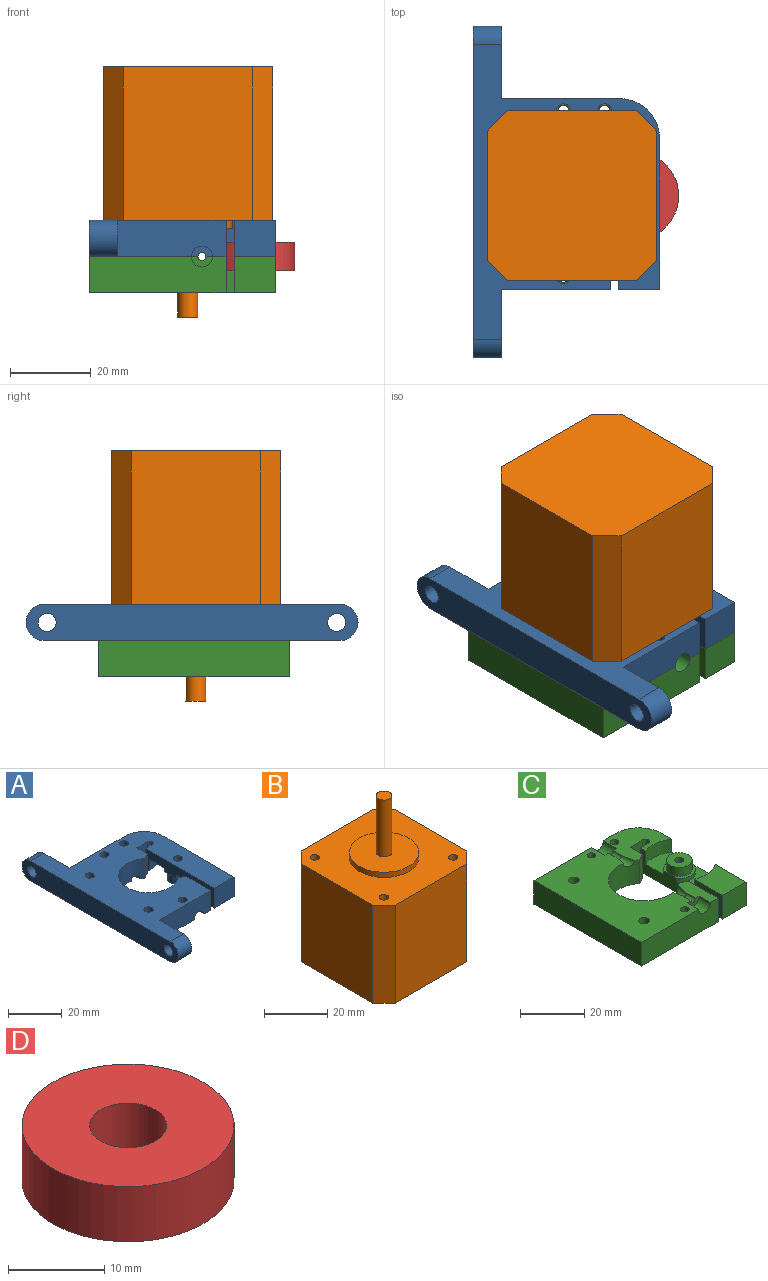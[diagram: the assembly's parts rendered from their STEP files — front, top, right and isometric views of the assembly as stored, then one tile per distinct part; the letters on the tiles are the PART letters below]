
ASSEMBLY  parts=4 mates=3
PART A: 50 faces, bbox 46.2x82.3x9 mm
  f0: plane 73.31x26.93mm, normal (0,0,-1), area 1150.4mm2, adj f3,f8,f9,f10,f15,f17,f21,f22
  f1: plane 14.38x4.98mm, normal (0,0,-1), area 58mm2, adj f3,f6,f10,f34,f35,f36,f37,f48
  f2: plane 17.27x15.32mm, normal (0,0,-1), area 170.8mm2, adj f3,f4,f5,f7,f8,f11,f12,f13
  f3: cylinder r=11.1mm len=22.2mm, axis (0,0,-1), area 433.2mm2, adj f0,f1,f2,f19,f33,f36,f48,f49
  f4: plane 36.35x9mm, normal (-1,0,0), area 219.3mm2, adj f2,f13,f14,f18,f19,f23,f24,f25
  f5: plane 37.28x9mm, normal (1,0,0), area 230.1mm2, adj f2,f14,f18,f19,f20,f23,f25,f26
  f6: plane 13.04x9mm, normal (1,0,0), area 111.2mm2, adj f1,f10,f19,f39,f48
  f7: plane 9x5.51mm, normal (1,0,0), area 49.5mm2, adj f2,f11,f19,f49
  f8: plane 29.2x9mm, normal (0,1,0), area 252.2mm2, adj f0,f2,f19,f20,f32,f43
  f9: plane 82.31x9mm, normal (-1,0,0), area 691.6mm2, adj f0,f19,f44,f45,f46,f47
  f10: plane 26.91x9mm, normal (0,-1,0), area 231.6mm2, adj f0,f1,f6,f19,f37,f42
  f11: plane 9x5.65mm, normal (0,-1,0), area 50.9mm2, adj f2,f7,f12,f19
  f12: cylinder r=1.22mm len=9mm, axis (0,0,1), area 34.6mm2, adj f2,f11,f13,f19
  f13: plane 9x3.65mm, normal (0,1,0), area 32.9mm2, adj f2,f4,f12,f19
  f14: plane 10.29x9mm, normal (0,-1,0), area 92.6mm2, adj f4,f5,f18,f19
  f15: cylinder r=1.7mm len=9mm, axis (0,0,1), area 96.1mm2, adj f0,f19
  f16: cylinder r=1.7mm len=9mm, axis (0,0,1), area 96.1mm2, adj f2,f19
  f17: cylinder r=1.7mm len=9mm, axis (0,0,1), area 96.1mm2, adj f0,f19
  f18: plane 13.53x10.29mm, normal (0,0,-1), area 124.8mm2, adj f4,f5,f14,f25
  f19: plane 73.31x46.2mm, normal (0,0,1), area 1816.6mm2, adj f3,f4,f5,f6,f7,f8,f9,f10
  f20: cylinder r=10mm len=10mm, axis (0,0,1), area 141.4mm2, adj f2,f5,f8,f19
  f21: cylinder r=1.7mm len=9mm, axis (0,0,-1), area 96.1mm2, adj f0,f19
  f22: cylinder r=1.7mm len=9mm, axis (0,0,-1), area 96.1mm2, adj f0,f19
  f23: cylinder r=11.5mm len=10.29mm, axis (0,0,-1), area 53.7mm2, adj f2,f4,f5,f26
  f24: cylinder r=5mm len=10mm, axis (0,0,-1), area 37.6mm2, adj f4,f26,f28
  f25: cylinder r=11.5mm len=10.29mm, axis (0,0,-1), area 53.7mm2, adj f4,f5,f18,f26
  f26: plane 23x10.29mm, normal (0,0,-1), area 152.7mm2, adj f4,f5,f23,f24,f25
  f27: cylinder r=4mm len=8mm, axis (0,0,-1), area 88mm2, adj f28,f29
  f28: plane 10x9.02mm, normal (0,0,-1), area 24.3mm2, adj f4,f24,f27
  f29: plane 8x8mm, normal (0,0,-1), area 41.2mm2, adj f27,f41
  f30: plane 5.2x2.6mm, normal (0,1,0), area 9mm2, adj f0,f2,f31,f32
  f31: cylinder r=1mm len=3.81mm, axis (0,-1,0), area 12mm2, adj f0,f2,f30,f33
  f32: cylinder r=2.6mm len=5.91mm, axis (0,-1,0), area 48.3mm2, adj f0,f2,f8,f30
  f33: cone r=1mm half-angle=12.4deg, axis (0,-1,0), area 18.5mm2, adj f0,f2,f3,f31
  f34: cylinder r=1mm len=3.81mm, axis (0,-1,0), area 12mm2, adj f0,f1,f35,f36
  f35: plane 5.2x2.6mm, normal (0,-1,0), area 9mm2, adj f0,f1,f34,f37
  f36: cone r=1mm half-angle=12.4deg, axis (0,1,0), area 18.5mm2, adj f0,f1,f3,f34
  f37: cylinder r=2.6mm len=5.2mm, axis (0,-1,0), area 40.6mm2, adj f0,f1,f10,f35
  f38: plane 2.8x2.8mm, normal (1,0,0), area 6.2mm2, adj f39
  f39: cylinder r=1.4mm len=7.71mm, axis (1,0,0), area 67.8mm2, adj f6,f38
  f40: cylinder r=1.7mm len=10.29mm, axis (1,0,0), area 109.9mm2, adj f4,f5
  f41: cylinder r=1.7mm len=9mm, axis (0,0,-1), area 96.1mm2, adj f19,f29
  f42: plane 17.03x9mm, normal (1,0,0), area 128.7mm2, adj f0,f10,f19,f44,f46
  f43: plane 18x9mm, normal (1,0,0), area 137.4mm2, adj f0,f8,f19,f45,f47
  f44: cylinder r=2.25mm len=7mm, axis (1,0,0), area 99mm2, adj f9,f42
  f45: cylinder r=2.25mm len=7mm, axis (1,0,0), area 99mm2, adj f9,f43
  f46: cylinder r=4.5mm len=9mm, axis (1,0,0), area 99mm2, adj f0,f9,f19,f42
  f47: cylinder r=4.5mm len=9mm, axis (-1,0,0), area 99mm2, adj f0,f9,f19,f43
  f48: plane 9x2.71mm, normal (0.44,0.9,0), area 27.2mm2, adj f1,f3,f6,f19
  f49: plane 9x2.71mm, normal (0.44,-0.9,0), area 27.2mm2, adj f2,f3,f7,f19
PART B: 22 faces, bbox 42x42x62 mm
  f0: plane 38x32mm, normal (-1,0,0), area 1216mm2, adj f4,f5,f8,f9
  f1: plane 38x32mm, normal (0,-1,0), area 1216mm2, adj f4,f5,f7,f9
  f2: plane 38x32mm, normal (1,0,0), area 1216mm2, adj f4,f5,f6,f7
  f3: plane 38x32mm, normal (0,1,0), area 1216mm2, adj f4,f5,f6,f8
  f4: plane 42x42mm, normal (0,0,1), area 1305.6mm2, adj f0,f1,f2,f3,f6,f7,f8,f9
  f5: plane 42x42mm, normal (0,0,-1), area 1714mm2, adj f0,f1,f2,f3,f6,f7,f8,f9
  f6: plane 38x5mm, normal (0.71,0.71,0), area 268.7mm2, adj f2,f3,f4,f5
  f7: plane 38x5mm, normal (0.71,-0.71,0), area 268.7mm2, adj f1,f2,f4,f5
  f8: plane 38x5mm, normal (-0.71,0.71,0), area 268.7mm2, adj f0,f3,f4,f5
  f9: plane 38x5mm, normal (-0.71,-0.71,0), area 268.7mm2, adj f0,f1,f4,f5
  f10: cylinder r=11mm len=22mm, axis (0,0,-1), area 138.2mm2, adj f4,f11
  f11: plane 22x22mm, normal (0,0,1), area 360.5mm2, adj f10,f12
  f12: cylinder r=2.5mm len=22mm, axis (0,0,-1), area 345.6mm2, adj f11,f13
  f13: plane 5x5mm, normal (0,0,1), area 19.6mm2, adj f12
  f14: cylinder r=1.5mm len=25mm, axis (0,0,1), area 235.6mm2, adj f4,f15
  f15: plane 3x3mm, normal (0,0,1), area 7.1mm2, adj f14
  f16: cylinder r=1.5mm len=25mm, axis (0,0,1), area 235.6mm2, adj f4,f17
  f17: plane 3x3mm, normal (0,0,1), area 7.1mm2, adj f16
  f18: cylinder r=1.5mm len=25mm, axis (0,0,1), area 235.6mm2, adj f4,f19
  f19: plane 3x3mm, normal (0,0,1), area 7.1mm2, adj f18
  f20: cylinder r=1.5mm len=25mm, axis (0,0,1), area 235.6mm2, adj f4,f21
  f21: plane 3x3mm, normal (0,0,1), area 7.1mm2, adj f20
PART C: 44 faces, bbox 46.2x47.3x9 mm
  f0: plane 47.28x26.93mm, normal (0,0,1), area 974.8mm2, adj f3,f7,f8,f9,f16,f18,f21,f22
  f1: plane 14.38x4.98mm, normal (0,0,1), area 58mm2, adj f3,f6,f9,f33,f34,f35,f36,f43
  f2: plane 17.27x15.32mm, normal (0,0,1), area 174.2mm2, adj f3,f4,f7,f10,f11,f12,f13,f15
  f3: cylinder r=11.1mm len=22.2mm, axis (0,0,1), area 433.2mm2, adj f0,f1,f2,f20,f32,f33,f42,f43
  f4: plane 36.35x9mm, normal (-1,0,0), area 219.3mm2, adj f2,f5,f13,f14,f19,f20,f23,f24
  f5: cylinder r=5mm len=10mm, axis (0,0,1), area 37.6mm2, adj f4,f25,f26
  f6: plane 13.04x9mm, normal (1,0,0), area 111.2mm2, adj f1,f9,f20,f38,f43
  f7: plane 36.2x9mm, normal (0,1,0), area 315.2mm2, adj f0,f2,f8,f20,f29,f37
  f8: plane 47.28x9mm, normal (-1,0,0), area 425.5mm2, adj f0,f7,f9,f20
  f9: plane 33.91x9mm, normal (0,-1,0), area 294.6mm2, adj f0,f1,f6,f8,f20,f36
  f10: plane 9x5.51mm, normal (1,0,0), area 49.5mm2, adj f2,f11,f20,f42
  f11: plane 9x5.65mm, normal (0,-1,0), area 50.9mm2, adj f2,f10,f12,f20
  f12: cylinder r=1.22mm len=9mm, axis (0,0,-1), area 34.6mm2, adj f2,f11,f13,f20
  f13: plane 9x3.65mm, normal (0,1,0), area 32.9mm2, adj f2,f4,f12,f20
  f14: plane 10.29x9mm, normal (0,-1,0), area 92.6mm2, adj f4,f17,f19,f20
  f15: cylinder r=1.35mm len=9mm, axis (0,0,-1), area 76.3mm2, adj f2,f20
  f16: cylinder r=1.35mm len=9mm, axis (0,0,-1), area 76.3mm2, adj f0,f20
  f17: plane 37.28x9mm, normal (1,0,0), area 230.1mm2, adj f2,f14,f19,f20,f23,f24,f25,f37
  f18: cylinder r=1.35mm len=9mm, axis (0,0,-1), area 76.3mm2, adj f0,f20
  f19: plane 13.53x10.29mm, normal (0,0,1), area 124.8mm2, adj f4,f14,f17,f24
  f20: plane 47.28x46.2mm, normal (0,0,-1), area 1647.4mm2, adj f3,f4,f6,f7,f8,f9,f10,f11
  f21: cylinder r=1.7mm len=9mm, axis (0,0,1), area 96.1mm2, adj f0,f20
  f22: cylinder r=1.7mm len=9mm, axis (0,0,1), area 96.1mm2, adj f0,f20
  f23: cylinder r=11.5mm len=10.29mm, axis (0,0,1), area 53.7mm2, adj f2,f4,f17,f25
  f24: cylinder r=11.5mm len=10.29mm, axis (0,0,1), area 53.7mm2, adj f4,f17,f19,f25
  f25: plane 23x10.29mm, normal (0,0,1), area 152.7mm2, adj f4,f5,f17,f23,f24
  f26: plane 10x9.02mm, normal (0,0,1), area 24.3mm2, adj f4,f5,f27
  f27: cylinder r=4mm len=8mm, axis (0,0,1), area 88mm2, adj f26,f28
  f28: plane 8x8mm, normal (0,0,1), area 44.1mm2, adj f27,f41
  f29: cylinder r=2.6mm len=5.91mm, axis (0,-1,0), area 48.3mm2, adj f0,f2,f7,f30
  f30: plane 5.2x2.6mm, normal (0,1,0), area 9mm2, adj f0,f2,f29,f31
  f31: cylinder r=1mm len=3.81mm, axis (0,-1,0), area 12mm2, adj f0,f2,f30,f32
  f32: cone r=1mm half-angle=12.4deg, axis (0,-1,0), area 18.5mm2, adj f0,f2,f3,f31
  f33: cone r=1mm half-angle=12.4deg, axis (0,1,0), area 18.5mm2, adj f0,f1,f3,f34
  f34: cylinder r=1mm len=3.81mm, axis (0,-1,0), area 12mm2, adj f0,f1,f33,f35
  f35: plane 5.2x2.6mm, normal (0,-1,0), area 9mm2, adj f0,f1,f34,f36
  f36: cylinder r=2.6mm len=5.2mm, axis (0,-1,0), area 40.6mm2, adj f0,f1,f9,f35
  f37: cylinder r=10mm len=10mm, axis (0,0,-1), area 141.4mm2, adj f2,f7,f17,f20
  f38: cylinder r=1.4mm len=7.71mm, axis (1,0,0), area 67.8mm2, adj f6,f39
  f39: plane 2.8x2.8mm, normal (1,0,0), area 6.2mm2, adj f38
  f40: cylinder r=1.7mm len=10.29mm, axis (1,0,0), area 109.9mm2, adj f4,f17
  f41: cylinder r=1.4mm len=9mm, axis (0,0,1), area 79.2mm2, adj f20,f28
  f42: plane 9x2.71mm, normal (0.44,-0.9,0), area 27.2mm2, adj f2,f3,f10,f20
  f43: plane 9x2.71mm, normal (0.44,0.9,0), area 27.2mm2, adj f1,f3,f6,f20
PART D: 4 faces, bbox 22x22x7 mm
  f0: cylinder r=4mm len=8mm, axis (0,0,-1), area 175.9mm2, adj f2,f3
  f1: cylinder r=11mm len=22mm, axis (0,0,-1), area 483.8mm2, adj f2,f3
  f2: plane 22x22mm, normal (0,0,1), area 329.9mm2, adj f0,f1
  f3: plane 22x22mm, normal (0,0,-1), area 329.9mm2, adj f0,f1
PLACE A t=(-37.06,-1.17,34.2)mm
PLACE B rot(axis=(0.71,-0.71,0),180deg) t=(-16.06,25.66,90.2)mm
PLACE C t=(-37.06,-1.17,34.2)mm
PLACE D t=(-21.56,4.66,39.7)mm
MATE fastened D.f0 <-> C.f5  axis (0,0,-1) through (-21.56,4.66,39.7)mm
MATE fastened B.f20 <-> A.f22  axis (0,0,-1) through (-52.56,20.16,52.2)mm
MATE fastened D.f0 <-> A.f23  axis (0,0,1) through (-21.56,4.66,46.7)mm
